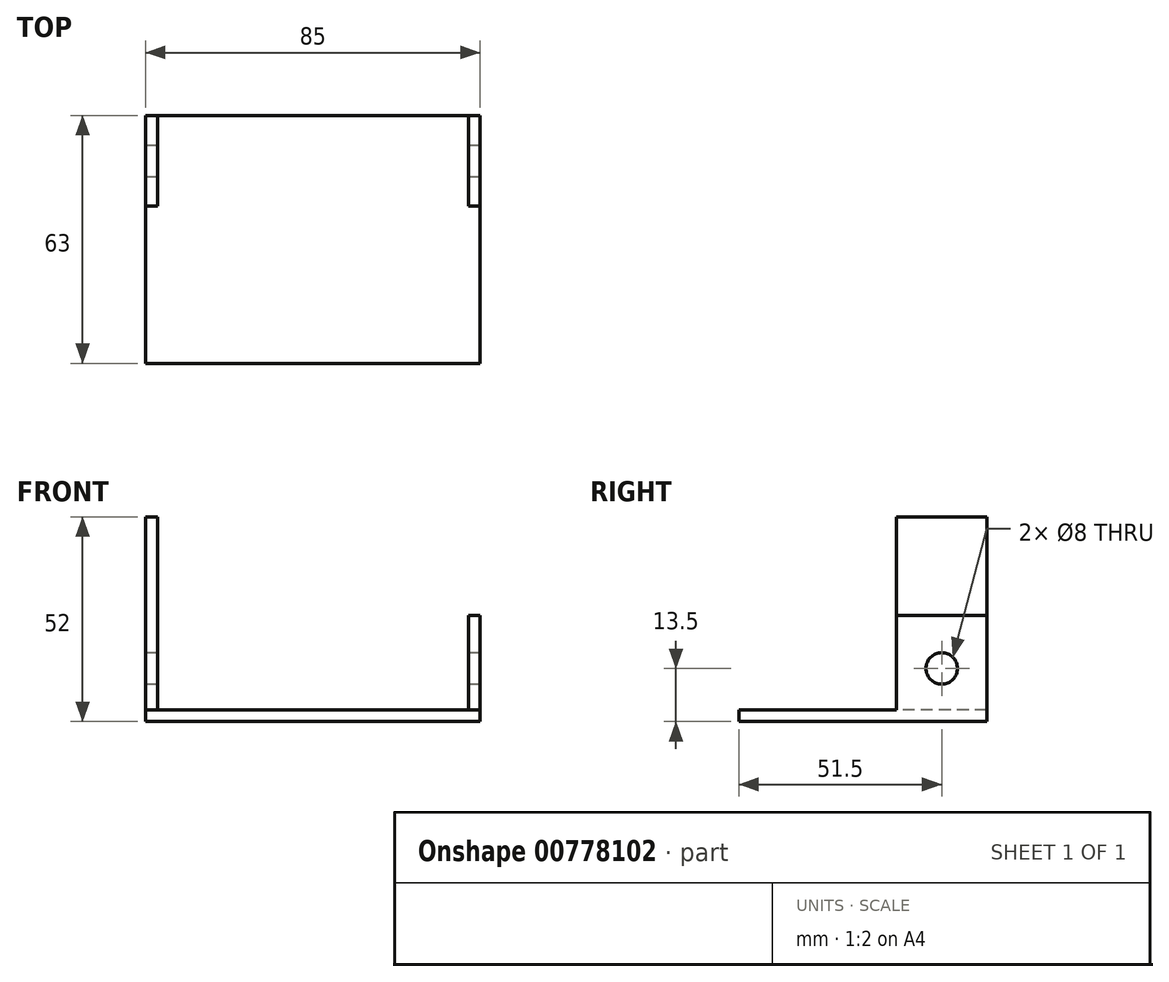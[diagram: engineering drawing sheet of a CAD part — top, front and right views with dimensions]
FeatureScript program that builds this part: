
annotation { "Feature Type Name" : "Feature", "Feature Type Description" : "" }
export const myFeature = defineFeature(function(context is Context, id is Id, definition is map)
    precondition{}
    {
        {
            var Q0;
            Q0=qCreatedBy(makeId("Top.planeOp"),FACE);
            var sketch = newSketch(context, id + "F0", { "sketchPlane" : qUnion([Q0])});
            skLineSegment(sketch, "E0.bottom", {"start": v(0, 0) * mm, "end": v(85, 0) * mm});
            skLineSegment(sketch, "E0.top", {"start": v(0, 23) * mm, "end": v(85, 23) * mm});
            skLineSegment(sketch, "E0.left", {"start": v(0, 0) * mm, "end": v(0, 23) * mm});
            skLineSegment(sketch, "E0.right", {"start": v(85, 0) * mm, "end": v(85, 23) * mm});
            skLineSegment(sketch, "E1.top", {"start": v(0, -40) * mm, "end": v(85, -40) * mm});
            skLineSegment(sketch, "E1.left", {"start": v(0, 0) * mm, "end": v(0, -40) * mm});
            skLineSegment(sketch, "E1.right", {"start": v(85, 0) * mm, "end": v(85, -40) * mm});
            skSolve(sketch);
        }
        {
            var Q0;
            Q0 = qSketchRegion(id + "F0", true);
            extrude(context, id + "F1", {"entities" : qUnion([Q0]), "depth" : 3 * mm, "offsetDistance" : 25 * mm});
        }
        {
            var Q0;
            Q0=makeQuery(id+"F1.opExtrude","CAP_FACE",FACE,{"disambiguationData":[OSD([sQuery(id+"F0.wireOp",EDGE,"E0.bottom"),sQuery(id+"F0.wireOp",EDGE,"E0.top"),sQuery(id+"F0.wireOp",EDGE,"E0.left"),sQuery(id+"F0.wireOp",EDGE,"E0.right")])],"isStart":false});
            var sketch = newSketch(context, id + "F2", { "sketchPlane" : qUnion([Q0])});
            skLineSegment(sketch, "E2.bottom", {"start": v(0, 23) * mm, "end": v(3, 23) * mm});
            skLineSegment(sketch, "E2.top", {"start": v(0, 0) * mm, "end": v(3, 0) * mm});
            skLineSegment(sketch, "E2.left", {"start": v(0, 23) * mm, "end": v(0, 0) * mm});
            skLineSegment(sketch, "E2.right", {"start": v(3, 23) * mm, "end": v(3, 0) * mm});
            skLineSegment(sketch, "E3.bottom", {"start": v(85, 23) * mm, "end": v(82, 23) * mm});
            skLineSegment(sketch, "E3.top", {"start": v(85, 0) * mm, "end": v(82, 0) * mm});
            skLineSegment(sketch, "E3.left", {"start": v(85, 23) * mm, "end": v(85, 0) * mm});
            skLineSegment(sketch, "E3.right", {"start": v(82, 23) * mm, "end": v(82, 0) * mm});
            skSolve(sketch);
        }
        {
            var Q0;
            Q0 = qSketchRegion(id + "F2", true);
            extrude(context, id + "F3", {"entities" : qUnion([Q0]), "operationType" : NewBodyOperationType.ADD, "depth" : 24 * mm, "offsetDistance" : 25 * mm});
        }
        {
            var Q0;
            Q0=makeQuery(id+"F3.opExtrude","CAP_FACE",FACE,{"disambiguationData":[OSD([sQuery(id+"F2.wireOp",EDGE,"E2.bottom"),sQuery(id+"F2.wireOp",EDGE,"E2.top"),sQuery(id+"F2.wireOp",EDGE,"E2.left"),sQuery(id+"F2.wireOp",EDGE,"E2.right")])],"isStart":false});
            var sketch = newSketch(context, id + "F4", { "sketchPlane" : qUnion([Q0])});
            skLineSegment(sketch, "E4.bottom", {"start": v(0, 23) * mm, "end": v(3, 23) * mm});
            skLineSegment(sketch, "E4.top", {"start": v(0, 0) * mm, "end": v(3, 0) * mm});
            skLineSegment(sketch, "E4.left", {"start": v(0, 23) * mm, "end": v(0, 0) * mm});
            skLineSegment(sketch, "E4.right", {"start": v(3, 23) * mm, "end": v(3, 0) * mm});
            skSolve(sketch);
        }
        {
            var Q0;
            Q0 = qSketchRegion(id + "F4", true);
            extrude(context, id + "F5", {"entities" : qUnion([Q0]), "operationType" : NewBodyOperationType.ADD, "depth" : 25 * mm, "offsetDistance" : 25 * mm});
        }
        {
            var Q0;
            Q0=makeQuery(id+"F3.boolean.opBoolean","MERGE",FACE,{"derivedFrom":[makeQuery(id+"F1.opExtrude","SWEPT_FACE",FACE,{"disambiguationData":[OSD([sQuery(id+"F0.wireOp",EDGE,"E0.right"),sQuery(id+"F0.wireOp",EDGE,"E1.right")])]}),makeQuery(id+"F3.opExtrude","SWEPT_FACE",FACE,{"disambiguationData":[OSD([sQuery(id+"F2.wireOp",EDGE,"E3.left")])]})]});
            var sketch = newSketch(context, id + "F6", { "sketchPlane" : qUnion([Q0])});
            skLineSegment(sketch, "E5", {"start": v(0, 27) * mm, "end": v(23, 0) * mm, "construction": true});
            skLineSegment(sketch, "E6", {"start": v(23, 0) * mm, "end": v(23, 27) * mm, "construction": true});
            skLineSegment(sketch, "E7", {"start": v(23, 27) * mm, "end": v(0, 0) * mm, "construction": true});
            skCircle(sketch, "E8", {"center": v(11.5, 13.5) * mm, "radius": 4 * mm});
            skSolve(sketch);
        }
        {
            var Q0;
            Q0 = qSketchRegion(id + "F6", true);
            extrude(context, id + "F7", {"entities" : qUnion([Q0]), "operationType" : NewBodyOperationType.REMOVE, "oppositeDirection" : true, "depth" : 200 * mm, "offsetDistance" : 25 * mm});
        }
    });
